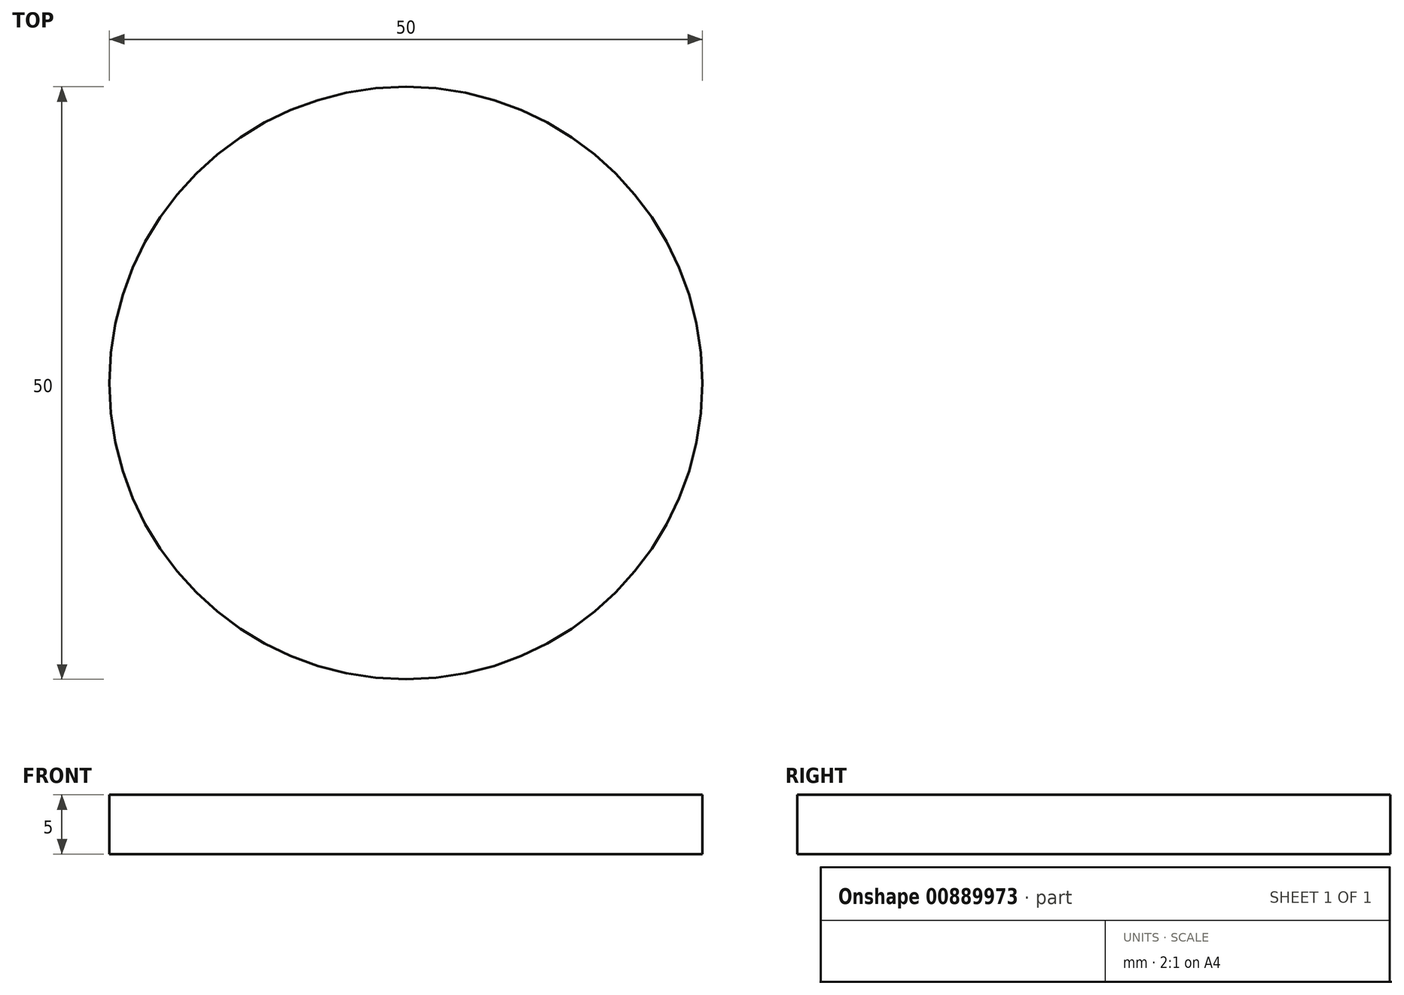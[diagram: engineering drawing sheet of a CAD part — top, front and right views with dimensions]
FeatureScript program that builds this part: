
annotation { "Feature Type Name" : "Feature", "Feature Type Description" : "" }
export const myFeature = defineFeature(function(context is Context, id is Id, definition is map)
    precondition{}
    {
        {
            var Q0;
            Q0=qCreatedBy(makeId("Top.planeOp"),FACE);
            var sketch = newSketch(context, id + "F0", { "sketchPlane" : qUnion([Q0])});
            skCircle(sketch, "E0", {"center": v(0, 0) * mm, "radius": 25 * mm});
            skSolve(sketch);
        }
        {
            var Q0;
            Q0=makeQuery(id+"F0.imprint","IMPRINT",FACE,{"disambiguationData":[TD([[makeQuery(id+"F0.imprint","IMPRINT",EDGE,{"derivedFrom":sQuery(id+"F0.wireOp",EDGE,"E0")}),1.0]])]});
            extrude(context, id + "F1", {"entities" : qUnion([Q0]), "depth" : 5 * mm, "offsetDistance" : 25.4 * mm});
        }
    });
